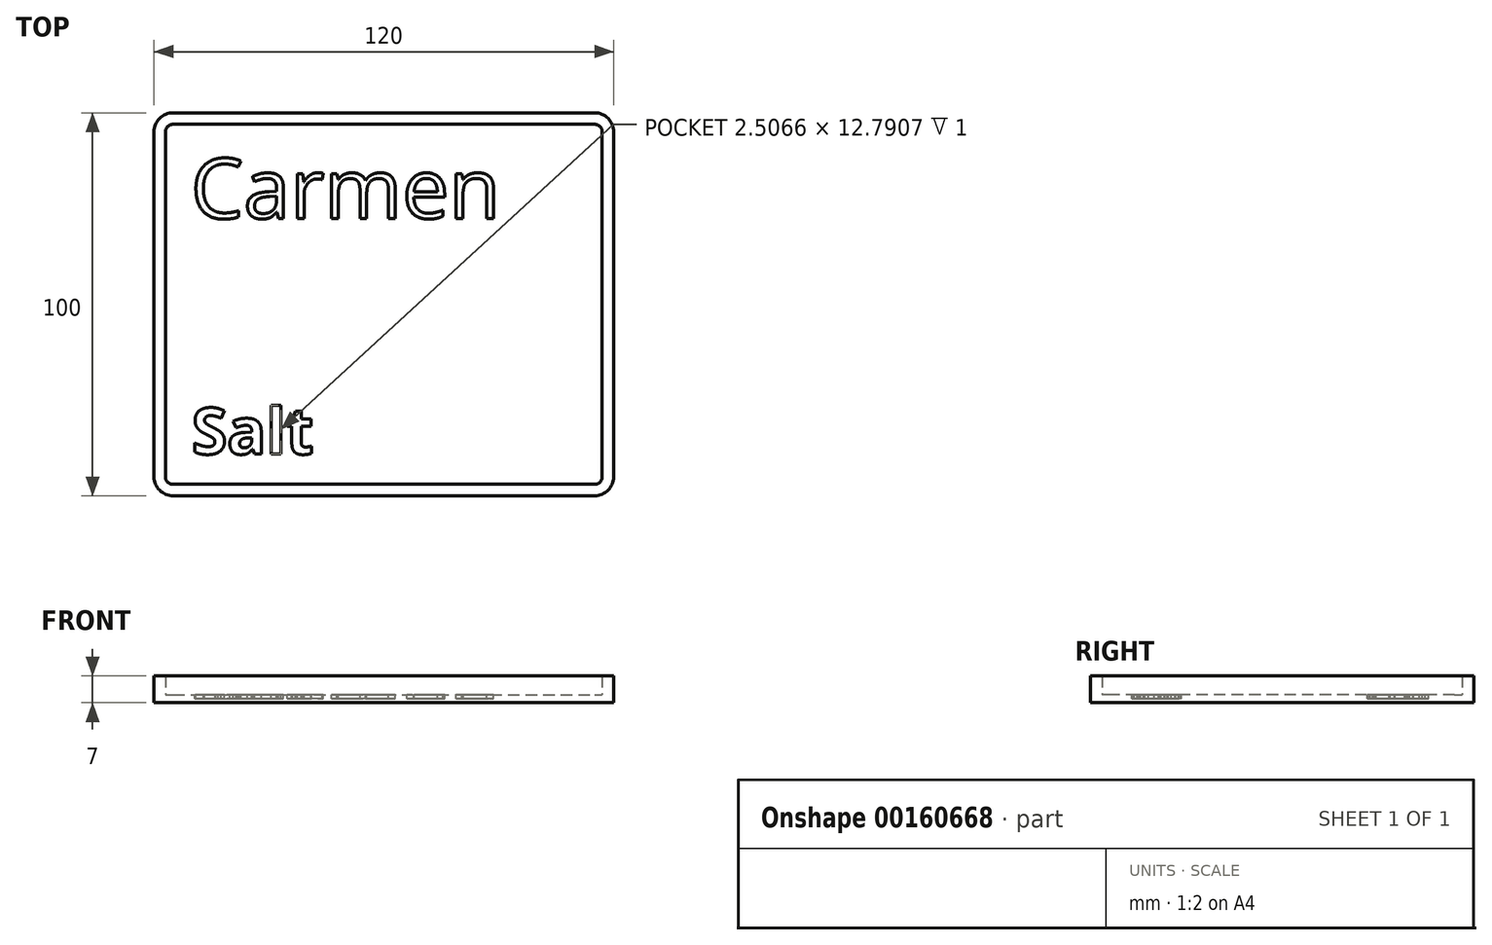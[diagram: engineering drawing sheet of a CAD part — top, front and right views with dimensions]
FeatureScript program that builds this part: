
annotation { "Feature Type Name" : "Feature", "Feature Type Description" : "" }
export const myFeature = defineFeature(function(context is Context, id is Id, definition is map)
    precondition{}
    {
        {
            var Q0;
            Q0=qCreatedBy(makeId("Top.planeOp"),FACE);
            var sketch = newSketch(context, id + "F0", { "sketchPlane" : qUnion([Q0])});
            skLineSegment(sketch, "E0.bottom", {"start": v(-60, 50) * mm, "end": v(60, 50) * mm});
            skLineSegment(sketch, "E0.top", {"start": v(-60, -50) * mm, "end": v(60, -50) * mm});
            skLineSegment(sketch, "E0.left", {"start": v(-60, 50) * mm, "end": v(-60, -50) * mm});
            skLineSegment(sketch, "E0.right", {"start": v(60, 50) * mm, "end": v(60, -50) * mm});
            skPoint(sketch, "E0.middle", {"position": v(0, 0) * mm});
            skSolve(sketch);
        }
        {
            var Q0;
            Q0=makeQuery(id+"F0.imprint","IMPRINT",FACE,{"disambiguationData":[TD([[makeQuery(id+"F0.imprint","IMPRINT",EDGE,{"derivedFrom":sQuery(id+"F0.wireOp",EDGE,"E0.bottom")}),-1.0]])]});
            extrude(context, id + "F1", {"entities" : qUnion([Q0]), "depth" : 2 * mm});
        }
        {
            var Q0;
            Q0=makeQuery(id+"F1.opExtrude","CAP_FACE",FACE,{"disambiguationData":[OSD([sQuery(id+"F0.wireOp",EDGE,"E0.bottom"),sQuery(id+"F0.wireOp",EDGE,"E0.top"),sQuery(id+"F0.wireOp",EDGE,"E0.left"),sQuery(id+"F0.wireOp",EDGE,"E0.right")])],"isStart":false});
            var sketch = newSketch(context, id + "F2", { "sketchPlane" : qUnion([Q0])});
            skLineSegment(sketch, "E1.0.0", {"start": v(60, 50) * mm, "end": v(-60, 50) * mm});
            skLineSegment(sketch, "E1.0.1", {"start": v(-60, 50) * mm, "end": v(-60, -50) * mm});
            skLineSegment(sketch, "E1.0.2", {"start": v(-60, -50) * mm, "end": v(60, -50) * mm});
            skLineSegment(sketch, "E1.0.3", {"start": v(60, -50) * mm, "end": v(60, 50) * mm});
            skLineSegment(sketch, "E2.0", {"start": v(57, 47) * mm, "end": v(-57, 47) * mm});
            skLineSegment(sketch, "E2.1", {"start": v(57, -47) * mm, "end": v(57, 47) * mm});
            skLineSegment(sketch, "E2.2", {"start": v(-57, -47) * mm, "end": v(57, -47) * mm});
            skLineSegment(sketch, "E2.3", {"start": v(-57, 47) * mm, "end": v(-57, -47) * mm});
            skSolve(sketch);
        }
        {
            var Q0;
            Q0=makeQuery(id+"F2.imprint","IMPRINT",FACE,{"disambiguationData":[TD([[makeQuery(id+"F2.imprint","IMPRINT",EDGE,{"derivedFrom":sQuery(id+"F2.wireOp",EDGE,"E1.0.0")}),-1.0]])]});
            extrude(context, id + "F3", {"entities" : qUnion([Q0]), "operationType" : NewBodyOperationType.ADD, "depth" : 5 * mm});
        }
        {
            var Q0;
            Q0=makeQuery(id+"F3.boolean.opBoolean","MERGE",EDGE,{"derivedFrom":[makeQuery(id+"F1.opExtrude","SWEPT_EDGE",EDGE,{"disambiguationData":[OSD([sQuery(id+"F0.wireOp",EDGE,"E0.top"),sQuery(id+"F0.wireOp",EDGE,"E0.left")])]}),makeQuery(id+"F3.opExtrude","SWEPT_EDGE",EDGE,{"disambiguationData":[OSD([sQuery(id+"F2.wireOp",EDGE,"E1.0.1"),sQuery(id+"F2.wireOp",EDGE,"E1.0.2")])]})]});
            var Q1;
            Q1=makeQuery(id+"F3.boolean.opBoolean","MERGE",EDGE,{"derivedFrom":[makeQuery(id+"F1.opExtrude","SWEPT_EDGE",EDGE,{"disambiguationData":[OSD([sQuery(id+"F0.wireOp",EDGE,"E0.top"),sQuery(id+"F0.wireOp",EDGE,"E0.right")])]}),makeQuery(id+"F3.opExtrude","SWEPT_EDGE",EDGE,{"disambiguationData":[OSD([sQuery(id+"F2.wireOp",EDGE,"E1.0.2"),sQuery(id+"F2.wireOp",EDGE,"E1.0.3")])]})]});
            var Q2;
            Q2=makeQuery(id+"F3.boolean.opBoolean","MERGE",EDGE,{"derivedFrom":[makeQuery(id+"F1.opExtrude","SWEPT_EDGE",EDGE,{"disambiguationData":[OSD([sQuery(id+"F0.wireOp",EDGE,"E0.bottom"),sQuery(id+"F0.wireOp",EDGE,"E0.right")])]}),makeQuery(id+"F3.opExtrude","SWEPT_EDGE",EDGE,{"disambiguationData":[OSD([sQuery(id+"F2.wireOp",EDGE,"E1.0.0"),sQuery(id+"F2.wireOp",EDGE,"E1.0.3")])]})]});
            var Q3;
            Q3=makeQuery(id+"F3.boolean.opBoolean","MERGE",EDGE,{"derivedFrom":[makeQuery(id+"F1.opExtrude","SWEPT_EDGE",EDGE,{"disambiguationData":[OSD([sQuery(id+"F0.wireOp",EDGE,"E0.bottom"),sQuery(id+"F0.wireOp",EDGE,"E0.left")])]}),makeQuery(id+"F3.opExtrude","SWEPT_EDGE",EDGE,{"disambiguationData":[OSD([sQuery(id+"F2.wireOp",EDGE,"E1.0.0"),sQuery(id+"F2.wireOp",EDGE,"E1.0.1")])]})]});
            fillet(context, id + "F4", {"entities" : qUnion([Q0, Q1, Q2, Q3]), "radius" : 5 * mm, "tangentPropagation" : true, "allowEdgeOverflow" : false});
        }
        {
            var Q0;
            Q0=makeQuery(id+"F3.opExtrude","SWEPT_EDGE",EDGE,{"disambiguationData":[OSD([sQuery(id+"F2.wireOp",EDGE,"E2.0"),sQuery(id+"F2.wireOp",EDGE,"E2.3")])]});
            var Q1;
            Q1=makeQuery(id+"F3.opExtrude","SWEPT_EDGE",EDGE,{"disambiguationData":[OSD([sQuery(id+"F2.wireOp",EDGE,"E2.0"),sQuery(id+"F2.wireOp",EDGE,"E2.1")])]});
            var Q2;
            Q2=makeQuery(id+"F3.opExtrude","SWEPT_EDGE",EDGE,{"disambiguationData":[OSD([sQuery(id+"F2.wireOp",EDGE,"E2.1"),sQuery(id+"F2.wireOp",EDGE,"E2.2")])]});
            var Q3;
            Q3=makeQuery(id+"F3.opExtrude","SWEPT_EDGE",EDGE,{"disambiguationData":[OSD([sQuery(id+"F2.wireOp",EDGE,"E2.2"),sQuery(id+"F2.wireOp",EDGE,"E2.3")])]});
            fillet(context, id + "F5", {"entities" : qUnion([Q0, Q1, Q2, Q3]), "radius" : 2 * mm, "tangentPropagation" : true, "allowEdgeOverflow" : false});
        }
        {
            var Q0;
            Q0=makeQuery(id+"F1.opExtrude","CAP_FACE",FACE,{"disambiguationData":[OSD([sQuery(id+"F0.wireOp",EDGE,"E0.bottom"),sQuery(id+"F0.wireOp",EDGE,"E0.top"),sQuery(id+"F0.wireOp",EDGE,"E0.left"),sQuery(id+"F0.wireOp",EDGE,"E0.right")])],"isStart":false});
            var sketch = newSketch(context, id + "F6", { "sketchPlane" : qUnion([Q0])});
            skText(sketch, "E3", { "text": "Carmen", "fontName": "OpenSans-Regular.ttf"});
            const initialGuessF6  = {"E3": [-0.05038, 0.02244, 1, 0, 0.01572]};
            skSetInitialGuess(sketch, initialGuessF6);
            skSolve(sketch);
        }
        {
            var Q0;
            Q0=makeQuery(id+"F1.opExtrude","CAP_FACE",FACE,{"disambiguationData":[OSD([sQuery(id+"F0.wireOp",EDGE,"E0.bottom"),sQuery(id+"F0.wireOp",EDGE,"E0.top"),sQuery(id+"F0.wireOp",EDGE,"E0.left"),sQuery(id+"F0.wireOp",EDGE,"E0.right")])],"isStart":false});
            var sketch = newSketch(context, id + "F7", { "sketchPlane" : qUnion([Q0])});
            skText(sketch, "E4", { "text": "Salt", "fontName": "OpenSans-Bold.ttf"});
            const initialGuessF7  = {"E4": [-0.05019, -0.03911, 1, 0, 0.01212]};
            skSetInitialGuess(sketch, initialGuessF7);
            skSolve(sketch);
        }
        {
            var Q0;
            Q0 = qSketchRegion(id + "F7", true);
            extrude(context, id + "F8", {"entities" : qUnion([Q0]), "operationType" : NewBodyOperationType.REMOVE, "oppositeDirection" : true, "depth" : 1 * mm});
        }
        {
            var Q0;
            Q0 = qSketchRegion(id + "F6", true);
            extrude(context, id + "F9", {"entities" : qUnion([Q0]), "operationType" : NewBodyOperationType.REMOVE, "oppositeDirection" : true, "depth" : 1 * mm, "offsetDistance" : 25 * mm});
        }
    });
